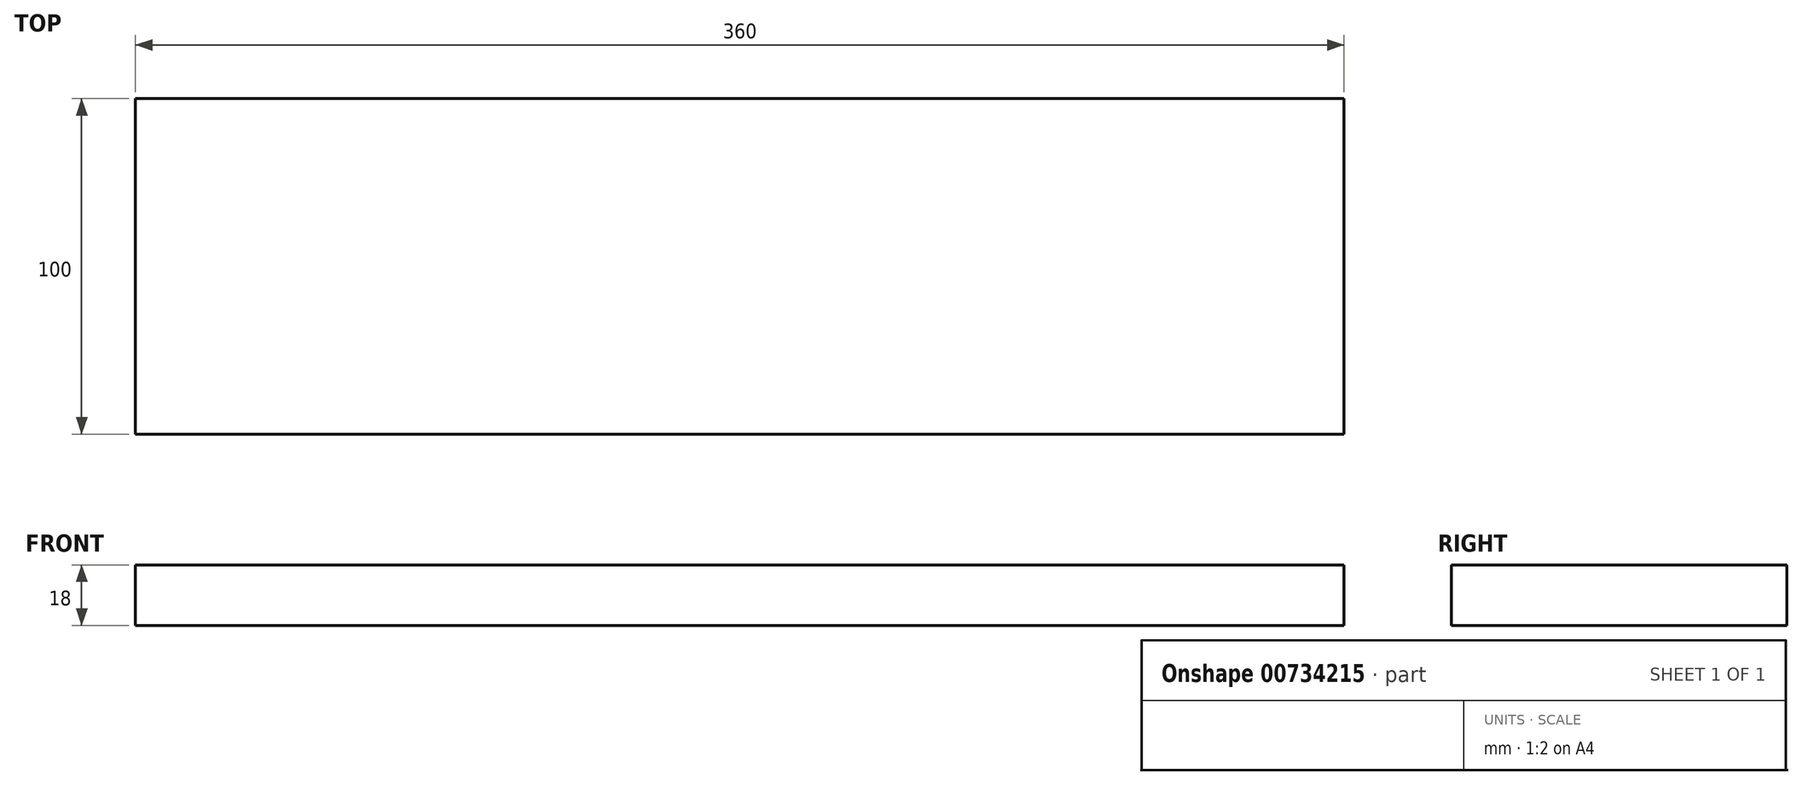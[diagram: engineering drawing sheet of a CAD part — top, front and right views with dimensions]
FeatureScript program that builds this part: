
annotation { "Feature Type Name" : "Feature", "Feature Type Description" : "" }
export const myFeature = defineFeature(function(context is Context, id is Id, definition is map)
    precondition{}
    {
        {
            var Q0;
            Q0=qCreatedBy(makeId("Top.planeOp"),FACE);
            var sketch = newSketch(context, id + "F0", { "sketchPlane" : qUnion([Q0])});
            skLineSegment(sketch, "E0.bottom", {"start": v(0, 0) * mm, "end": v(360, 0) * mm});
            skLineSegment(sketch, "E0.top", {"start": v(0, 100) * mm, "end": v(360, 100) * mm});
            skLineSegment(sketch, "E0.left", {"start": v(0, 0) * mm, "end": v(0, 100) * mm});
            skLineSegment(sketch, "E0.right", {"start": v(360, 0) * mm, "end": v(360, 100) * mm});
            skSolve(sketch);
        }
        {
            var Q0;
            Q0=makeQuery(id+"F0.imprint","IMPRINT",FACE,{"disambiguationData":[TD([[makeQuery(id+"F0.imprint","IMPRINT",EDGE,{"derivedFrom":sQuery(id+"F0.wireOp",EDGE,"E0.bottom")}),1.0]])]});
            extrude(context, id + "F1", {"entities" : qUnion([Q0]), "depth" : 18 * mm, "offsetDistance" : 25 * mm});
        }
    });
